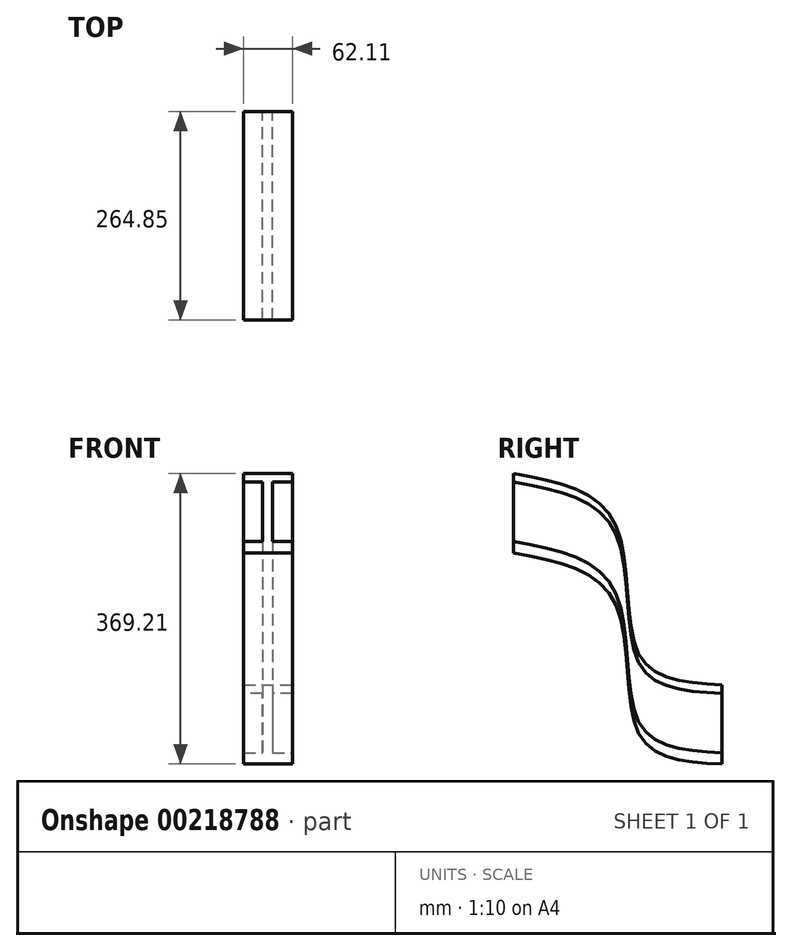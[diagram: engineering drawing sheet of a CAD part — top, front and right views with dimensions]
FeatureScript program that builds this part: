
annotation { "Feature Type Name" : "Feature", "Feature Type Description" : "" }
export const myFeature = defineFeature(function(context is Context, id is Id, definition is map)
    precondition{}
    {
        {
            var Q0;
            Q0=qCreatedBy(makeId("Front.planeOp"),FACE);
            var sketch = newSketch(context, id + "F0", { "sketchPlane" : qUnion([Q0])});
            skLineSegment(sketch, "E0", {"start": v(-33.02, 56.23) * mm, "end": v(29.1, 56.23) * mm});
            skLineSegment(sketch, "E1", {"start": v(29.1, 56.23) * mm, "end": v(29.1, 45.37) * mm});
            skLineSegment(sketch, "E2", {"start": v(29.1, 45.37) * mm, "end": v(3.93, 45.37) * mm});
            skLineSegment(sketch, "E3", {"start": v(3.93, 45.37) * mm, "end": v(3.93, -30.13) * mm});
            skLineSegment(sketch, "E4", {"start": v(3.93, -30.13) * mm, "end": v(29.1, -30.13) * mm});
            skLineSegment(sketch, "E5", {"start": v(29.1, -30.13) * mm, "end": v(29.1, -44.45) * mm});
            skLineSegment(sketch, "E6", {"start": v(29.1, -44.45) * mm, "end": v(-33.02, -44.45) * mm});
            skLineSegment(sketch, "E7", {"start": v(-33.02, -44.45) * mm, "end": v(-33.02, -30.13) * mm});
            skLineSegment(sketch, "E8", {"start": v(-33.02, -30.13) * mm, "end": v(-9.24, -30.13) * mm});
            skLineSegment(sketch, "E9", {"start": v(-9.24, -30.13) * mm, "end": v(-9.24, 45.37) * mm});
            skLineSegment(sketch, "E10", {"start": v(-9.24, 45.37) * mm, "end": v(-33.02, 45.37) * mm});
            skLineSegment(sketch, "E11", {"start": v(-33.02, 45.37) * mm, "end": v(-33.02, 56.23) * mm});
            skSolve(sketch);
        }
        {
            var Q0;
            Q0=qCreatedBy(makeId("Right.planeOp"),FACE);
            var sketch = newSketch(context, id + "F1", { "sketchPlane" : qUnion([Q0])});
            skFitSpline(sketch, "E12", {"points": [v(0, 0) * mm, v(128.28, -61.73) * mm, v(160.96, -232.65) * mm, v(264.85, -268.53) * mm], "startDerivative": vector(477.2, -88.98) * mm, "endDerivative": vector(434.54, -23.38) * mm});
            skSolve(sketch);
        }
        {
            var Q0;
            Q0=makeQuery(id+"F0.imprint","IMPRINT",FACE,{"disambiguationData":[TD([[makeQuery(id+"F0.imprint","IMPRINT",EDGE,{"derivedFrom":sQuery(id+"F0.wireOp",EDGE,"E0")}),-1.0]])]});
            var Q1;
            Q1=sQuery(id+"F1.wireOp",EDGE,"E12");
            sweep(context, id + "F2", {"profiles" : qUnion([Q0]), "path" : qUnion([Q1]), "keepProfileOrientation" : true});
        }
    });
